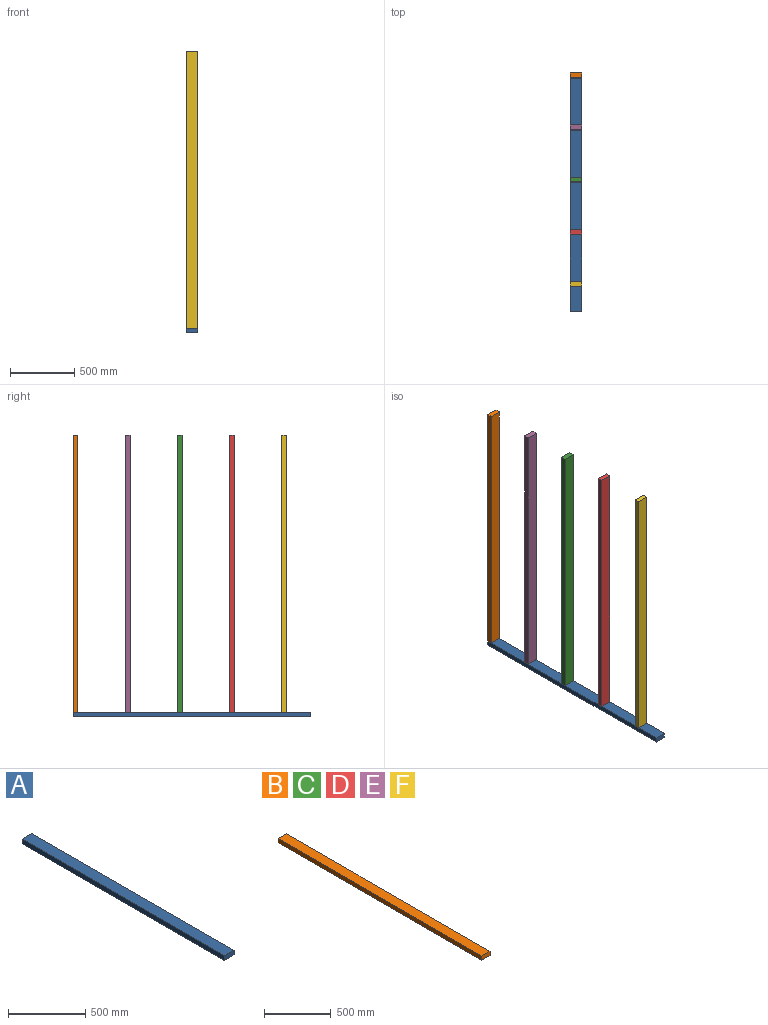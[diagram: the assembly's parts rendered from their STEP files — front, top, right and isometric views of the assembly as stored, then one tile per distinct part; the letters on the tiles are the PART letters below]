
ASSEMBLY  parts=6 mates=1
PART A: 6 faces, bbox 88.9x1854.2x38.1 mm
  f0: plane 1854.2x38.1mm, normal (-1,0,0), area 70645mm2, adj f1,f3,f4,f5
  f1: plane 1854.2x88.9mm, normal (0,0,-1), area 164838.4mm2, adj f0,f2,f4,f5
  f2: plane 1854.2x38.1mm, normal (1,0,0), area 70645mm2, adj f1,f3,f4,f5
  f3: plane 1854.2x88.9mm, normal (0,0,1), area 164838.4mm2, adj f0,f2,f4,f5
  f4: plane 88.9x38.1mm, normal (0,-1,0), area 3387.1mm2, adj f0,f1,f2,f3
  f5: plane 88.9x38.1mm, normal (0,1,0), area 3387.1mm2, adj f0,f1,f2,f3
PART B: 6 faces, bbox 88.9x2159x38.1 mm
  f0: plane 2159x38.1mm, normal (-1,0,0), area 82257.9mm2, adj f1,f3,f4,f5
  f1: plane 2159x88.9mm, normal (0,0,-1), area 191935.1mm2, adj f0,f2,f4,f5
  f2: plane 2159x38.1mm, normal (1,0,0), area 82257.9mm2, adj f1,f3,f4,f5
  f3: plane 2159x88.9mm, normal (0,0,1), area 191935.1mm2, adj f0,f2,f4,f5
  f4: plane 88.9x38.1mm, normal (0,-1,0), area 3387.1mm2, adj f0,f1,f2,f3
  f5: plane 88.9x38.1mm, normal (0,1,0), area 3387.1mm2, adj f0,f1,f2,f3
PART C: same geometry as B
PART D: same geometry as B
PART E: same geometry as B
PART F: same geometry as B
PLACE A t=(219.74,2159,0)mm
PLACE B rot(axis=(-1,0,0),90deg) t=(219.74,-38.1,38.1)mm
PLACE C rot(axis=(-1,0,0),90deg) t=(219.74,-850.9,38.1)mm
PLACE D rot(axis=(-1,0,0),90deg) t=(219.74,-1257.3,38.1)mm
PLACE E rot(axis=(-1,0,0),90deg) t=(219.74,-444.5,38.1)mm
PLACE F rot(axis=(-1,0,0),90deg) t=(219.74,-1663.7,38.1)mm
MATE fastened A.f3 <-> B.f5  axis (0,0,1) through (0,0,38.1)mm
